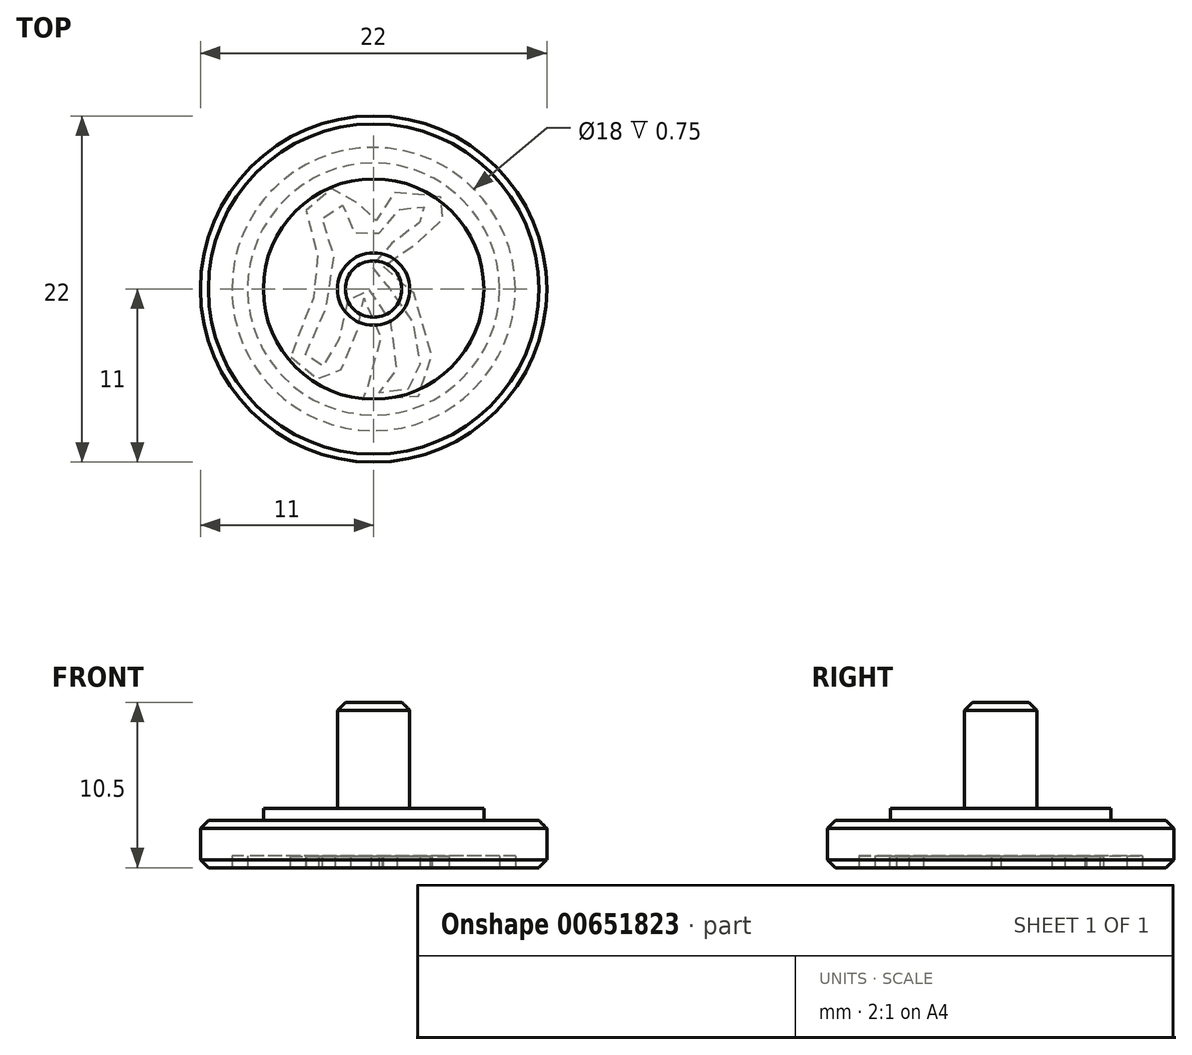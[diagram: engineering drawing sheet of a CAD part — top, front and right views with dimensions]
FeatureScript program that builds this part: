
annotation { "Feature Type Name" : "Feature", "Feature Type Description" : "" }
export const myFeature = defineFeature(function(context is Context, id is Id, definition is map)
    precondition{}
    {
        {
            var Q0;
            Q0=qCreatedBy(makeId("Top.planeOp"),FACE);
            var sketch = newSketch(context, id + "F0", { "sketchPlane" : qUnion([Q0])});
            skCircle(sketch, "E0", {"center": v(0, 0) * mm, "radius": 11 * mm});
            skCircle(sketch, "E1", {"center": v(0, 0) * mm, "radius": 7 * mm});
            skCircle(sketch, "E2", {"center": v(0, 0) * mm, "radius": 3.9 * mm});
            skCircle(sketch, "E3", {"center": v(0, 0) * mm, "radius": 2.3 * mm});
            skSolve(sketch);
        }
        {
            var Q0;
            Q0=makeQuery(id+"F0.imprint","IMPRINT",FACE,{"disambiguationData":[TD([[makeQuery(id+"F0.imprint","IMPRINT",EDGE,{"derivedFrom":sQuery(id+"F0.wireOp",EDGE,"E0")}),1.0]])]});
            extrude(context, id + "F1", {"entities" : qUnion([Q0]), "depth" : 3 * mm, "offsetDistance" : 25.4 * mm});
        }
        {
            var Q0;
            Q0=makeQuery(id+"F0.imprint","IMPRINT",FACE,{"disambiguationData":[TD([[makeQuery(id+"F0.imprint","IMPRINT",EDGE,{"derivedFrom":sQuery(id+"F0.wireOp",EDGE,"E1")}),1.0]])]});
            var Q1;
            Q1=makeQuery(id+"F0.imprint","IMPRINT",FACE,{"disambiguationData":[TD([[makeQuery(id+"F0.imprint","IMPRINT",EDGE,{"derivedFrom":sQuery(id+"F0.wireOp",EDGE,"E2")}),1.0]])]});
            extrude(context, id + "F2", {"entities" : qUnion([Q0, Q1]), "operationType" : NewBodyOperationType.ADD, "depth" : 3.75 * mm, "offsetDistance" : 25.4 * mm});
        }
        {
            var Q0;
            Q0=makeQuery(id+"F0.imprint","IMPRINT",FACE,{"disambiguationData":[TD([[makeQuery(id+"F0.imprint","IMPRINT",EDGE,{"derivedFrom":sQuery(id+"F0.wireOp",EDGE,"E2")}),1.0]])]});
            extrude(context, id + "F3", {"entities" : qUnion([Q0]), "depth" : 3.75 * mm, "offsetDistance" : 25.4 * mm});
        }
        {
            var Q0;
            Q0=makeQuery(id+"F0.imprint","IMPRINT",FACE,{"disambiguationData":[TD([[makeQuery(id+"F0.imprint","IMPRINT",EDGE,{"derivedFrom":sQuery(id+"F0.wireOp",EDGE,"E3")}),1.0]])]});
            extrude(context, id + "F4", {"entities" : qUnion([Q0]), "depth" : 10.5 * mm, "offsetDistance" : 25.4 * mm});
        }
        {
            var Q0;
            Q0=makeQuery(id+"F0.imprint","IMPRINT",FACE,{"disambiguationData":[TD([[makeQuery(id+"F0.imprint","IMPRINT",EDGE,{"derivedFrom":sQuery(id+"F0.wireOp",EDGE,"E3")}),1.0]])]});
            extrude(context, id + "F5", {"entities" : qUnion([Q0]), "operationType" : NewBodyOperationType.ADD, "depth" : 3.75 * mm, "offsetDistance" : 25.4 * mm});
        }
        {
            var Q0;
            Q0=qCreatedBy(makeId("Top.planeOp"),FACE);
            var sketch = newSketch(context, id + "F6", { "sketchPlane" : qUnion([Q0])});
            skCircle(sketch, "E4", {"center": v(0, 0) * mm, "radius": 9 * mm});
            skCircle(sketch, "E5", {"center": v(0, 0) * mm, "radius": 8 * mm});
            skFitSpline(sketch, "E6", {"points": [v(-5.25, -4.32) * mm, v(-3.91, -5.5) * mm, v(-2.87, -5.8) * mm, v(-1.88, -4.87) * mm, v(-0.98, -2.31) * mm, v(-0.7, -0.6) * mm, v(0, -1.38) * mm, v(0, -6) * mm, v(-1.47, -6.84) * mm, v(2.19, -6.99) * mm, v(3.55, -5.77) * mm, v(2.65, -0.4) * mm, v(0.62, 1.37) * mm, v(2.45, 2.68) * mm, v(3.96, 4.08) * mm, v(4.77, 4.92) * mm, v(4.36, 5.79) * mm, v(1.34, 6.14) * mm, v(0.53, 4.77) * mm, v(-0.57, 4.13) * mm, v(-1.27, 6.25) * mm, v(-2.96, 6.28) * mm, v(-4.26, 5.2) * mm, v(-3.6, 2.3) * mm, v(-3.74, -0.3) * mm, v(-4.58, -2.55) * mm, v(-5.13, -3.65) * mm, v(-5.25, -4.32) * mm]});
            skFitSpline(sketch, "E7", {"points": [v(-4.32, -4.15) * mm, v(-2.8, -0.66) * mm, v(-2.67, 2.69) * mm, v(-3.27, 4.56) * mm, v(-2.67, 5.15) * mm, v(-1.8, 5.27) * mm, v(-1.38, 3.83) * mm, v(-0.51, 3.24) * mm, v(0.42, 3.59) * mm, v(1.4, 4.63) * mm, v(1.98, 5.4) * mm, v(3.12, 5.26) * mm, v(3.58, 4.93) * mm, v(3.08, 4.36) * mm, v(1.91, 3.36) * mm, v(0.3, 2.32) * mm, v(-0.14, 1.38) * mm, v(0.34, 0.6) * mm, v(1.87, -0.87) * mm, v(2.71, -3.03) * mm, v(2.9, -5.3) * mm, v(2.43, -6.23) * mm, v(1.2, -6.57) * mm, v(0.35, -6.6) * mm, v(1.22, -5.83) * mm, v(1.31, -3.2) * mm, v(0.44, -0.48) * mm, v(-0.8, 0) * mm, v(-1.52, -0.47) * mm, v(-1.92, -2.25) * mm, v(-2.7, -4.28) * mm, v(-3.25, -4.91) * mm, v(-3.89, -4.63) * mm, v(-4.32, -4.15) * mm]});
            skSolve(sketch);
        }
        {
            var Q0;
            Q0=makeQuery(id+"F6.imprint","IMPRINT",FACE,{"disambiguationData":[TD([[makeQuery(id+"F6.imprint","IMPRINT",EDGE,{"derivedFrom":sQuery(id+"F6.wireOp",EDGE,"E4")}),1.0]])]});
            extrude(context, id + "F7", {"entities" : qUnion([Q0]), "operationType" : NewBodyOperationType.REMOVE, "depth" : 0.75 * mm, "offsetDistance" : 25.4 * mm});
        }
        {
            var Q0;
            Q0=makeQuery(id+"F6.imprint","IMPRINT",FACE,{"disambiguationData":[TD([[makeQuery(id+"F6.imprint","IMPRINT",EDGE,{"derivedFrom":sQuery(id+"F6.wireOp",EDGE,"E6")}),1.0]])]});
            extrude(context, id + "F8", {"entities" : qUnion([Q0]), "operationType" : NewBodyOperationType.REMOVE, "depth" : 0.7 * mm, "offsetDistance" : 25.4 * mm});
        }
        {
            var Q0;
            Q0=makeQuery(id+"F3.opExtrude","CAP_EDGE",EDGE,{"disambiguationData":[OSD([sQuery(id+"F0.wireOp",EDGE,"E3")])],"isStart":false});
            var Q1;
            Q1=makeQuery(id+"F1.opExtrude","CAP_EDGE",EDGE,{"disambiguationData":[OSD([sQuery(id+"F0.wireOp",EDGE,"E0")])],"isStart":false});
            var Q2;
            Q2=makeQuery(id+"F1.opExtrude","CAP_EDGE",EDGE,{"disambiguationData":[OSD([sQuery(id+"F0.wireOp",EDGE,"E0")])],"isStart":true});
            chamfer(context, id + "F9", {"entities" : qUnion([Q0, Q1, Q2]), "width" : 0.5 * mm, "tangentPropagation" : true});
        }
        {
            var Q0;
            Q0=makeQuery(id+"F6.imprint","IMPRINT",FACE,{"disambiguationData":[TD([[makeQuery(id+"F6.imprint","IMPRINT",EDGE,{"derivedFrom":sQuery(id+"F6.wireOp",EDGE,"E7")}),-1.0]])]});
            extrude(context, id + "F10", {"entities" : qUnion([Q0]), "operationType" : NewBodyOperationType.ADD, "depth" : 1 * mm, "offsetDistance" : 25.4 * mm});
        }
        {
            var Q0;
            Q0=makeQuery(id+"F6.imprint","IMPRINT",FACE,{"disambiguationData":[TD([[makeQuery(id+"F6.imprint","IMPRINT",EDGE,{"derivedFrom":sQuery(id+"F6.wireOp",EDGE,"E6")}),1.0]])]});
            extrude(context, id + "F11", {"entities" : qUnion([Q0]), "operationType" : NewBodyOperationType.REMOVE, "depth" : 0.7 * mm, "offsetDistance" : 25.4 * mm});
        }
        {
            var Q0;
            Q0=makeQuery(id+"F6.imprint","IMPRINT",FACE,{"disambiguationData":[TD([[makeQuery(id+"F6.imprint","IMPRINT",EDGE,{"derivedFrom":sQuery(id+"F6.wireOp",EDGE,"E6")}),1.0]])]});
            extrude(context, id + "F12", {"entities" : qUnion([Q0]), "operationType" : NewBodyOperationType.REMOVE, "depth" : 0.7 * mm, "offsetDistance" : 25.4 * mm});
        }
        {
            var Q0;
            Q0=makeQuery(id+"F4.opExtrude","CAP_EDGE",EDGE,{"disambiguationData":[OSD([sQuery(id+"F0.wireOp",EDGE,"E3")])],"isStart":false});
            chamfer(context, id + "F13", {"entities" : qUnion([Q0]), "width" : 0.5 * mm, "tangentPropagation" : true});
        }
    });
